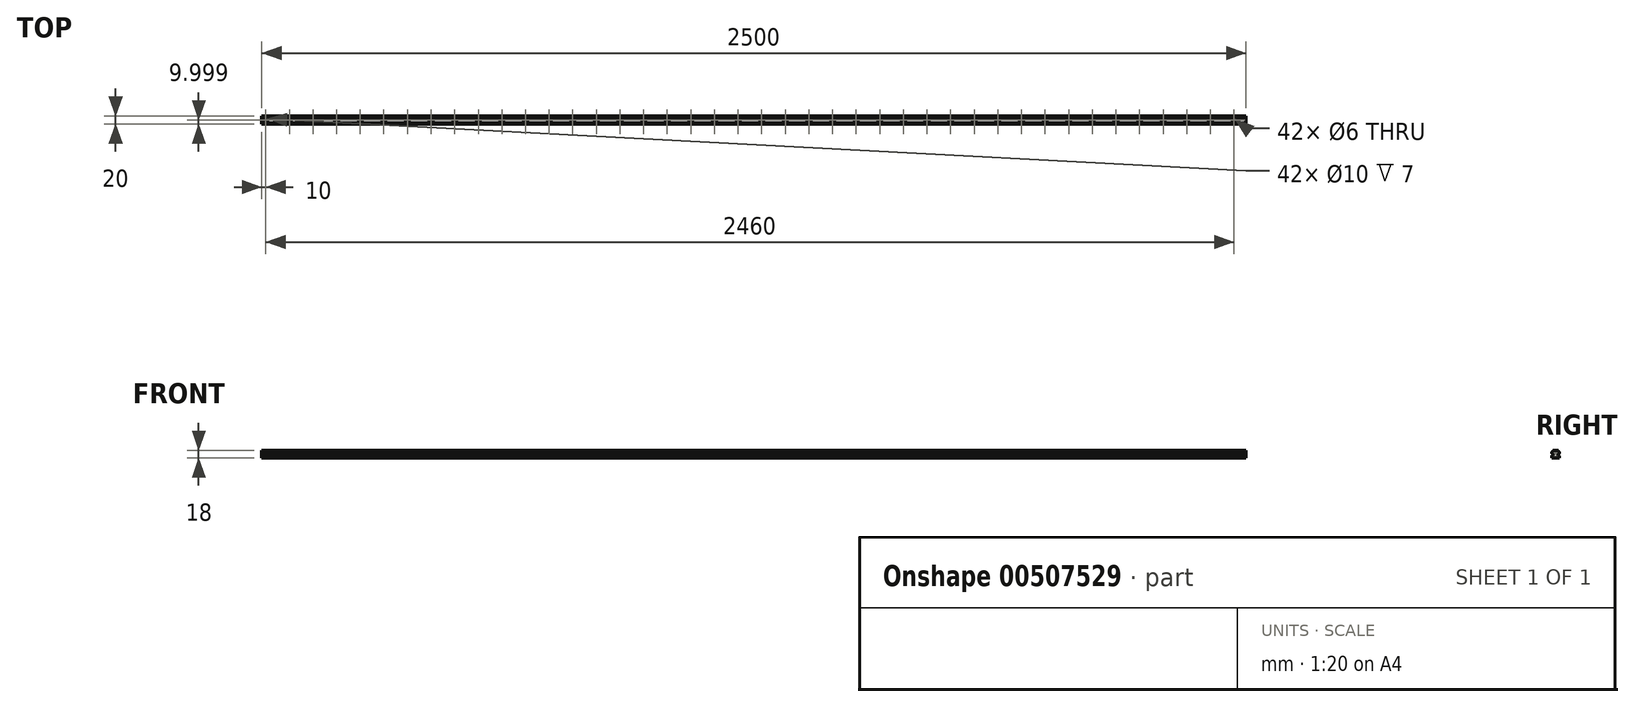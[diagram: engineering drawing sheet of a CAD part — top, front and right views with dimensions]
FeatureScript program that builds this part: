
annotation { "Feature Type Name" : "Feature", "Feature Type Description" : "" }
export const myFeature = defineFeature(function(context is Context, id is Id, definition is map)
    precondition{}
    {
        {
            var Q0;
            Q0=qCreatedBy(makeId("Right.planeOp"),FACE);
            var sketch = newSketch(context, id + "F0", { "sketchPlane" : qUnion([Q0])});
            skLineSegment(sketch, "E0", {"start": v(-26.04, 0) * mm, "end": v(-26.04, 5) * mm});
            skLineSegment(sketch, "E1", {"start": v(-26.04, 11) * mm, "end": v(-26.04, 15) * mm});
            skLineSegment(sketch, "E2", {"start": v(-23.04, 18) * mm, "end": v(-9.04, 18) * mm});
            skLineSegment(sketch, "E3", {"start": v(-6.04, 15) * mm, "end": v(-6.04, 11) * mm});
            skLineSegment(sketch, "E4", {"start": v(-6.04, 5) * mm, "end": v(-6.04, 0) * mm});
            skLineSegment(sketch, "E5", {"start": v(-6.04, 0) * mm, "end": v(-26.04, 0) * mm});
            skArc(sketch, "E6", {"start": v(-26.04, 5) * mm, "mid": v(-23.04, 8) * mm, "end": v(-26.04, 11) * mm});
            skArc(sketch, "E7", {"start": v(-6.04, 11) * mm, "mid": v(-9.04, 8) * mm, "end": v(-6.04, 5) * mm});
            skArc(sketch, "E8", {"start": v(-26.04, 15) * mm, "mid": v(-23.92, 15.88) * mm, "end": v(-23.04, 18) * mm});
            skArc(sketch, "E9", {"start": v(-9.04, 18) * mm, "mid": v(-8.16, 15.88) * mm, "end": v(-6.04, 15) * mm});
            skSolve(sketch);
        }
        {
            var Q0;
            Q0 = qSketchRegion(id + "F0", true);
            extrude(context, id + "F1", {"entities" : qUnion([Q0]), "flatOperationType" : FlatOperationType.REMOVE, "offsetDistance" : 25 * mm, "depth" : 2500 * mm, "domain" : OperationDomain.MODEL});
        }
        {
            var Q0;
            Q0=makeQuery(id+"F1.opExtrude","SWEPT_FACE",FACE,{"disambiguationData":[OSD([sQuery(id+"F0.wireOp",EDGE,"E2")])]});
            var sketch = newSketch(context, id + "F2", { "sketchPlane" : qUnion([Q0])});
            skCircle(sketch, "E10", {"center": v(10, -16.04) * mm, "radius": 3 * mm});
            skCircle(sketch, "E11", {"center": v(70, -16.04) * mm, "radius": 3 * mm});
            skCircle(sketch, "E12", {"center": v(130, -16.04) * mm, "radius": 3 * mm});
            skCircle(sketch, "E13", {"center": v(190, -16.04) * mm, "radius": 3 * mm});
            skCircle(sketch, "E14", {"center": v(250, -16.04) * mm, "radius": 3 * mm});
            skCircle(sketch, "E15", {"center": v(310, -16.04) * mm, "radius": 3 * mm});
            skCircle(sketch, "E16", {"center": v(370, -16.04) * mm, "radius": 3 * mm});
            skCircle(sketch, "E17", {"center": v(430, -16.04) * mm, "radius": 3 * mm});
            skCircle(sketch, "E18", {"center": v(490, -16.04) * mm, "radius": 3 * mm});
            skCircle(sketch, "E19", {"center": v(550, -16.04) * mm, "radius": 3 * mm});
            skCircle(sketch, "E20", {"center": v(610, -16.04) * mm, "radius": 3 * mm});
            skCircle(sketch, "E21", {"center": v(670, -16.04) * mm, "radius": 3 * mm});
            skCircle(sketch, "E22", {"center": v(730, -16.04) * mm, "radius": 3 * mm});
            skCircle(sketch, "E23", {"center": v(790, -16.04) * mm, "radius": 3 * mm});
            skCircle(sketch, "E24", {"center": v(850, -16.04) * mm, "radius": 3 * mm});
            skCircle(sketch, "E25", {"center": v(910, -16.04) * mm, "radius": 3 * mm});
            skCircle(sketch, "E26", {"center": v(970, -16.04) * mm, "radius": 3 * mm});
            skCircle(sketch, "E27", {"center": v(1030, -16.04) * mm, "radius": 3 * mm});
            skCircle(sketch, "E28", {"center": v(1090, -16.04) * mm, "radius": 3 * mm});
            skCircle(sketch, "E29", {"center": v(1150, -16.04) * mm, "radius": 3 * mm});
            skCircle(sketch, "E30", {"center": v(1210, -16.04) * mm, "radius": 3 * mm});
            skCircle(sketch, "E31", {"center": v(1270, -16.04) * mm, "radius": 3 * mm});
            skCircle(sketch, "E32", {"center": v(1330, -16.04) * mm, "radius": 3 * mm});
            skCircle(sketch, "E33", {"center": v(1390, -16.04) * mm, "radius": 3 * mm});
            skCircle(sketch, "E34", {"center": v(1450, -16.04) * mm, "radius": 3 * mm});
            skCircle(sketch, "E35", {"center": v(1510, -16.04) * mm, "radius": 3 * mm});
            skCircle(sketch, "E36", {"center": v(1570, -16.04) * mm, "radius": 3 * mm});
            skCircle(sketch, "E37", {"center": v(1630, -16.04) * mm, "radius": 3 * mm});
            skCircle(sketch, "E38", {"center": v(1690, -16.04) * mm, "radius": 3 * mm});
            skCircle(sketch, "E39", {"center": v(1750, -16.04) * mm, "radius": 3 * mm});
            skCircle(sketch, "E40", {"center": v(1810, -16.04) * mm, "radius": 3 * mm});
            skCircle(sketch, "E41", {"center": v(1870, -16.04) * mm, "radius": 3 * mm});
            skCircle(sketch, "E42", {"center": v(1930, -16.04) * mm, "radius": 3 * mm});
            skCircle(sketch, "E43", {"center": v(1990, -16.04) * mm, "radius": 3 * mm});
            skCircle(sketch, "E44.0.1.0", {"center": v(2050, -16.04) * mm, "radius": 3 * mm});
            skCircle(sketch, "E44.0.2.0", {"center": v(2110, -16.04) * mm, "radius": 3 * mm});
            skCircle(sketch, "E44.0.3.0", {"center": v(2170, -16.04) * mm, "radius": 3 * mm});
            skCircle(sketch, "E44.0.4.0", {"center": v(2230, -16.04) * mm, "radius": 3 * mm});
            skCircle(sketch, "E44.0.5.0", {"center": v(2290, -16.04) * mm, "radius": 3 * mm});
            skCircle(sketch, "E44.0.6.0", {"center": v(2350, -16.04) * mm, "radius": 3 * mm});
            skCircle(sketch, "E44.0.7.0", {"center": v(2410, -16.04) * mm, "radius": 3 * mm});
            skCircle(sketch, "E44.0.8.0", {"center": v(2470, -16.04) * mm, "radius": 3 * mm});
            skLineSegment(sketch, "E44.direction1", {"start": v(1990, -16.04) * mm, "end": v(2050, -16.04) * mm, "construction": true});
            skSolve(sketch);
        }
        {
            var Q0;
            Q0 = qSketchRegion(id + "F2", true);
            extrude(context, id + "F3", {"entities" : qUnion([Q0]), "operationType" : NewBodyOperationType.REMOVE, "oppositeDirection" : true, "depth" : 18 * mm});
        }
        {
            var Q0;
            Q0=makeQuery(id+"F1.opExtrude","SWEPT_FACE",FACE,{"disambiguationData":[OSD([sQuery(id+"F0.wireOp",EDGE,"E2")])]});
            var sketch = newSketch(context, id + "F4", { "sketchPlane" : qUnion([Q0])});
            skCircle(sketch, "E45", {"center": v(10, -16.04) * mm, "radius": 5 * mm});
            skCircle(sketch, "E46", {"center": v(70, -16.04) * mm, "radius": 5 * mm});
            skCircle(sketch, "E47", {"center": v(130, -16.04) * mm, "radius": 5 * mm});
            skCircle(sketch, "E48", {"center": v(190, -16.04) * mm, "radius": 5 * mm});
            skCircle(sketch, "E49", {"center": v(250, -16.04) * mm, "radius": 5 * mm});
            skCircle(sketch, "E50", {"center": v(310, -16.04) * mm, "radius": 5 * mm});
            skCircle(sketch, "E51", {"center": v(370, -16.04) * mm, "radius": 5 * mm});
            skCircle(sketch, "E52", {"center": v(430, -16.04) * mm, "radius": 5 * mm});
            skCircle(sketch, "E53", {"center": v(490, -16.04) * mm, "radius": 5 * mm});
            skCircle(sketch, "E54", {"center": v(550, -16.04) * mm, "radius": 5 * mm});
            skCircle(sketch, "E55", {"center": v(610, -16.04) * mm, "radius": 5 * mm});
            skCircle(sketch, "E56", {"center": v(670, -16.04) * mm, "radius": 5 * mm});
            skCircle(sketch, "E57", {"center": v(730, -16.04) * mm, "radius": 5 * mm});
            skCircle(sketch, "E58", {"center": v(790, -16.04) * mm, "radius": 5 * mm});
            skCircle(sketch, "E59", {"center": v(850, -16.04) * mm, "radius": 5 * mm});
            skCircle(sketch, "E60", {"center": v(910, -16.04) * mm, "radius": 5 * mm});
            skCircle(sketch, "E61", {"center": v(970, -16.04) * mm, "radius": 5 * mm});
            skCircle(sketch, "E62", {"center": v(1030, -16.04) * mm, "radius": 5 * mm});
            skCircle(sketch, "E63", {"center": v(1090, -16.04) * mm, "radius": 5 * mm});
            skCircle(sketch, "E64", {"center": v(1150, -16.04) * mm, "radius": 5 * mm});
            skCircle(sketch, "E65", {"center": v(1210, -16.04) * mm, "radius": 5 * mm});
            skCircle(sketch, "E66", {"center": v(1270, -16.04) * mm, "radius": 5 * mm});
            skCircle(sketch, "E67", {"center": v(1330, -16.04) * mm, "radius": 5 * mm});
            skCircle(sketch, "E68", {"center": v(1390, -16.04) * mm, "radius": 5 * mm});
            skCircle(sketch, "E69", {"center": v(1450, -16.04) * mm, "radius": 5 * mm});
            skCircle(sketch, "E70", {"center": v(1510, -16.04) * mm, "radius": 5 * mm});
            skCircle(sketch, "E71", {"center": v(1570, -16.04) * mm, "radius": 5 * mm});
            skCircle(sketch, "E72", {"center": v(1630, -16.04) * mm, "radius": 5 * mm});
            skCircle(sketch, "E73", {"center": v(1690, -16.04) * mm, "radius": 5 * mm});
            skCircle(sketch, "E74", {"center": v(1750, -16.04) * mm, "radius": 5 * mm});
            skCircle(sketch, "E75", {"center": v(1810, -16.04) * mm, "radius": 5 * mm});
            skCircle(sketch, "E76", {"center": v(1870, -16.04) * mm, "radius": 5 * mm});
            skCircle(sketch, "E77", {"center": v(1930, -16.04) * mm, "radius": 5 * mm});
            skCircle(sketch, "E78", {"center": v(1990, -16.04) * mm, "radius": 5 * mm});
            skCircle(sketch, "E79.0.1.0", {"center": v(2050, -16.04) * mm, "radius": 5 * mm});
            skCircle(sketch, "E79.0.2.0", {"center": v(2110, -16.04) * mm, "radius": 5 * mm});
            skCircle(sketch, "E79.0.3.0", {"center": v(2170, -16.04) * mm, "radius": 5 * mm});
            skCircle(sketch, "E79.0.4.0", {"center": v(2230, -16.04) * mm, "radius": 5 * mm});
            skCircle(sketch, "E79.0.5.0", {"center": v(2290, -16.04) * mm, "radius": 5 * mm});
            skCircle(sketch, "E79.0.6.0", {"center": v(2350, -16.04) * mm, "radius": 5 * mm});
            skCircle(sketch, "E79.0.7.0", {"center": v(2410, -16.04) * mm, "radius": 5 * mm});
            skCircle(sketch, "E79.0.8.0", {"center": v(2470, -16.04) * mm, "radius": 5 * mm});
            skLineSegment(sketch, "E79.direction1", {"start": v(1990, -16.04) * mm, "end": v(2050, -16.04) * mm, "construction": true});
            skSolve(sketch);
        }
        {
            var Q0;
            Q0 = qSketchRegion(id + "F4", true);
            extrude(context, id + "F5", {"entities" : qUnion([Q0]), "operationType" : NewBodyOperationType.REMOVE, "oppositeDirection" : true, "depth" : 7 * mm});
        }
    });
